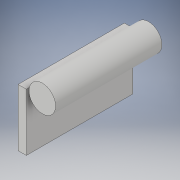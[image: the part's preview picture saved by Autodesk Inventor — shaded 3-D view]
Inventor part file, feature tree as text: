
AUTODESK INVENTOR PART (.ipt)
format: ipt  version: 2019 (Build 230136000, 136)  size: 98,816 bytes
history: native  units: mm
features: extrude x1, sketch x1
ambient origin geometry x8: Origin, YZ Plane, XZ Plane, XY Plane, X Axis, Y Axis, Z Axis, Center Point
bodies: Solid1 (feature_tree)
feature tree (2):
  extrude  "Extrusion1"  Depth=200.0mm TaperAngle=0.0deg
  sketch  "Sketch1"  dims[d0=50.0mm d5=200.0mm d6=0.0mm d7=112.0mm d8=30.0mm]
